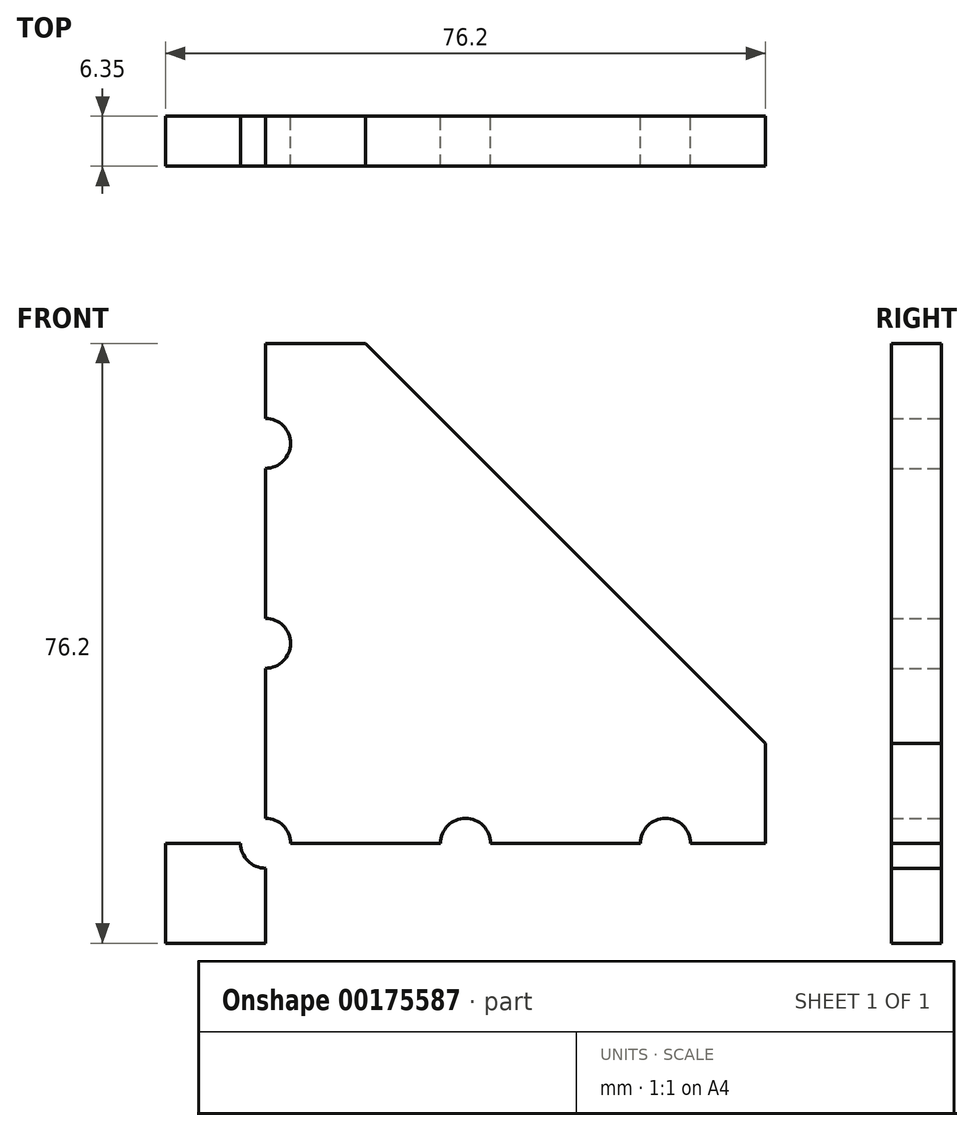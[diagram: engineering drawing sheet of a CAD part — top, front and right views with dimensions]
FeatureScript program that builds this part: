
annotation { "Feature Type Name" : "Feature", "Feature Type Description" : "" }
export const myFeature = defineFeature(function(context is Context, id is Id, definition is map)
    precondition{}
    {
        {
            var Q0;
            Q0=qCreatedBy(makeId("Front.planeOp"),FACE);
            var sketch = newSketch(context, id + "F0", { "sketchPlane" : qUnion([Q0])});
            skLineSegment(sketch, "E0.bottom", {"start": v(38.1, 38.1) * mm, "end": v(-38.1, 38.1) * mm});
            skLineSegment(sketch, "E0.top", {"start": v(38.1, -38.1) * mm, "end": v(-38.1, -38.1) * mm});
            skLineSegment(sketch, "E0.left", {"start": v(38.1, 38.1) * mm, "end": v(38.1, -38.1) * mm});
            skLineSegment(sketch, "E0.right", {"start": v(-38.1, 38.1) * mm, "end": v(-38.1, -38.1) * mm});
            skPoint(sketch, "E0.middle", {"position": v(0, 0) * mm});
            skLineSegment(sketch, "E1", {"start": v(-38.1, 38.1) * mm, "end": v(-12.7, 38.1) * mm});
            skLineSegment(sketch, "E2", {"start": v(38.1, -38.1) * mm, "end": v(38.1, -12.7) * mm});
            skLineSegment(sketch, "E3", {"start": v(-12.7, 38.1) * mm, "end": v(38.1, -12.7) * mm});
            skLineSegment(sketch, "E4", {"start": v(-25.4, 38.1) * mm, "end": v(-25.4, -38.1) * mm});
            skLineSegment(sketch, "E5", {"start": v(-38.1, -25.4) * mm, "end": v(38.1, -25.4) * mm});
            skCircle(sketch, "E6", {"center": v(-25.4, -25.4) * mm, "radius": 3.18 * mm});
            skCircle(sketch, "E7", {"center": v(0, -25.4) * mm, "radius": 3.18 * mm});
            skCircle(sketch, "E8", {"center": v(25.4, -25.4) * mm, "radius": 3.18 * mm});
            skCircle(sketch, "E9", {"center": v(-25.4, 0) * mm, "radius": 3.18 * mm});
            skCircle(sketch, "E10", {"center": v(-25.4, 25.4) * mm, "radius": 3.18 * mm});
            skSolve(sketch);
        }
        {
            var Q0;
            {var subQ21=sQuery(id+"F0.wireOp",EDGE,"E3");Q0=makeQuery(id+"F0.imprint","IMPRINT",FACE,{"disambiguationData":[TD([[makeQuery(id+"F0.imprint","IMPRINT",EDGE,{"derivedFrom":subQ21}),-1.0]])]});}
            var Q1;
            {var subQ5=sQuery(id+"F0.wireOp",EDGE,"E1");var subQ6=sQuery(id+"F0.wireOp",EDGE,"E0.right");var subQ7=makeQuery(id+"F0.imprint","INTERSECT",VERTEX,{"derivedFrom":[subQ6,subQ5]});Q1=makeQuery(id+"F0.imprint","IMPRINT",FACE,{"disambiguationData":[TD([[makeQuery(id+"F0.imprint","IMPRINT",EDGE,{"disambiguationData":[TD([[subQ7,-1.0]])],"derivedFrom":subQ6}),1.0]])]});}
            var Q2;
            {var subQ1=sQuery(id+"F0.wireOp",EDGE,"E0.right");var subQ5=sQuery(id+"F0.wireOp",EDGE,"E0.top");var subQ6=makeQuery(id+"F0.imprint","INTERSECT",VERTEX,{"derivedFrom":[subQ5,subQ1]});Q2=makeQuery(id+"F0.imprint","IMPRINT",FACE,{"disambiguationData":[TD([[makeQuery(id+"F0.imprint","IMPRINT",EDGE,{"disambiguationData":[TD([[subQ6,1.0]])],"derivedFrom":subQ5}),-1.0]])]});}
            var Q3;
            {var subQ5=sQuery(id+"F0.wireOp",EDGE,"E2");var subQ6=sQuery(id+"F0.wireOp",EDGE,"E0.top");var subQ7=makeQuery(id+"F0.imprint","INTERSECT",VERTEX,{"derivedFrom":[subQ6,subQ5]});Q3=makeQuery(id+"F0.imprint","IMPRINT",FACE,{"disambiguationData":[TD([[makeQuery(id+"F0.imprint","IMPRINT",EDGE,{"disambiguationData":[TD([[subQ7,-1.0]])],"derivedFrom":subQ6}),-1.0]])]});}
            extrude(context, id + "F1", {"entities" : qUnion([Q0, Q1, Q2, Q3]), "depth" : 6.35 * mm});
        }
    });
